FCSTD DOCUMENT  (FreeCAD 0.18R4 (GitTag))
Label: tank e
License: All rights reserved
LicenseURL: http://en.wikipedia.org/wiki/All_rights_reserved
objects: App::FeaturePython×8, Part::Part2DObjectPython×4, Part::Feature×3
note: 7 computed .brp shape members not serialized (recipe doc carries the construction recipe); baked Part::Feature solids carry a one-line shape summary decoded from their .brp

FEATURE [Part::Part2DObjectPython] Circle  # Draft 2D object (typed FeaturePython)
  FirstAngle = 0
  LastAngle = 0
  MakeFace = true
  Placement = pos=(-165,221,0) rot=(0,0,1;0rad)
  Radius = 7.5
FEATURE [Part::Part2DObjectPython] Circle001  # Draft 2D object (typed FeaturePython)
  FirstAngle = 0
  LastAngle = 0
  MakeFace = true
  Placement = pos=(-165,61,0) rot=(0,0,1;0rad)
  Radius = 10
FEATURE [Part::Feature] Wire
  Placement = pos=(40,11,0) rot=(0,0,1;0rad)
  shape: bbox 240 x 250 x 2e-07 mm, 0 faces, 0 solids (baked)
FEATURE [App::FeaturePython] Dimension  # Draft dimension (typed FeaturePython)
  Diameter = false
  Dimline = (-144.314,240.608,0)
  Direction = (0,0,0)
  Distance = 40.6971
  End = (-165,261,0)
  Normal = (0,0,1)
  Start = (-172.5,221,0)
FEATURE [App::FeaturePython] Dimension002  # Draft dimension (typed FeaturePython)
  Diameter = false
  Dimline = (-180.31,31.8361,0)
  Direction = (0,0,0)
  Distance = 50.9902
  End = (-165,11,0)
  Normal = (0,0,1)
  Start = (-175,61,0)
FEATURE [Part::Feature] Wire001
  Placement = pos=(-260,11,0) rot=(0,0,1;0rad)
  shape: bbox 240 x 250 x 2e-07 mm, 0 faces, 0 solids (baked)
FEATURE [Part::Part2DObjectPython] Circle002  # Draft 2D object (typed FeaturePython)
  FirstAngle = 0
  LastAngle = 0
  MakeFace = true
  Placement = pos=(135,61,0) rot=(0,0,1;0rad)
  Radius = 10
FEATURE [App::FeaturePython] Dimension004  # Draft dimension (typed FeaturePython)
  Diameter = false
  Dimline = (121.916,18.6251,0)
  Direction = (0,0,0)
  Distance = 50.9902
  End = (135,11,0)
  Normal = (0,0,1)
  Start = (125,61,0)
FEATURE [App::FeaturePython] Dimension005  # Draft dimension (typed FeaturePython)
  Diameter = false
  Dimline = (42.283,73.6816,0)
  Direction = (0,0,0)
  Distance = 99.747
  End = (35.253,61.0637,0)
  Normal = (0,0,1)
  Start = (135,61,0)
FEATURE [App::FeaturePython] Dimension006  # Draft dimension (typed FeaturePython)
  Diameter = false
  Dimline = (-278.799,207.385,0)
  Direction = (0,0,0)
  Distance = 115.986
  End = (-280.986,220.83,0)
  Normal = (0,0,1)
  Start = (-165,221,0)
FEATURE [App::FeaturePython] Dimension007  # Draft dimension (typed FeaturePython)
  Diameter = false
  Dimline = (-262.995,77.7926,0)
  Direction = (0,0,0)
  Distance = 99.9775
  End = (-264.977,61.1365,0)
  Normal = (0,0,1)
  Start = (-165,61,0)
FEATURE [Part::Part2DObjectPython] Circle003  # Draft 2D object (typed FeaturePython)
  FirstAngle = 0
  LastAngle = 0
  MakeFace = true
  Placement = pos=(-150.261,-149.381,0) rot=(0,0,1;0rad)
  Radius = 11
FEATURE [Part::Feature] Wire002
  Placement = pos=(-270.261,-269.381,0) rot=(0,0,1;0rad)
  shape: bbox 240 x 240 x 2e-07 mm, 0 faces, 0 solids (baked)
FEATURE [App::FeaturePython] Dimension008  # Draft dimension (typed FeaturePython)
  Diameter = false
  Dimline = (-34.1571,-163.451,0)
  Direction = (0,0,0)
  Distance = 120
  End = (-30.2607,-149.381,0)
  Normal = (0,0,1)
  Start = (-150.261,-149.381,0)
FEATURE [App::FeaturePython] Dimension009  # Draft dimension (typed FeaturePython)
  Diameter = false
  Dimline = (-164.026,-36.5751,0)
  Direction = (0,0,0)
  Distance = 120
  End = (-150.261,-29.3808,0)
  Normal = (0,0,1)
  Start = (-150.261,-149.381,0)
